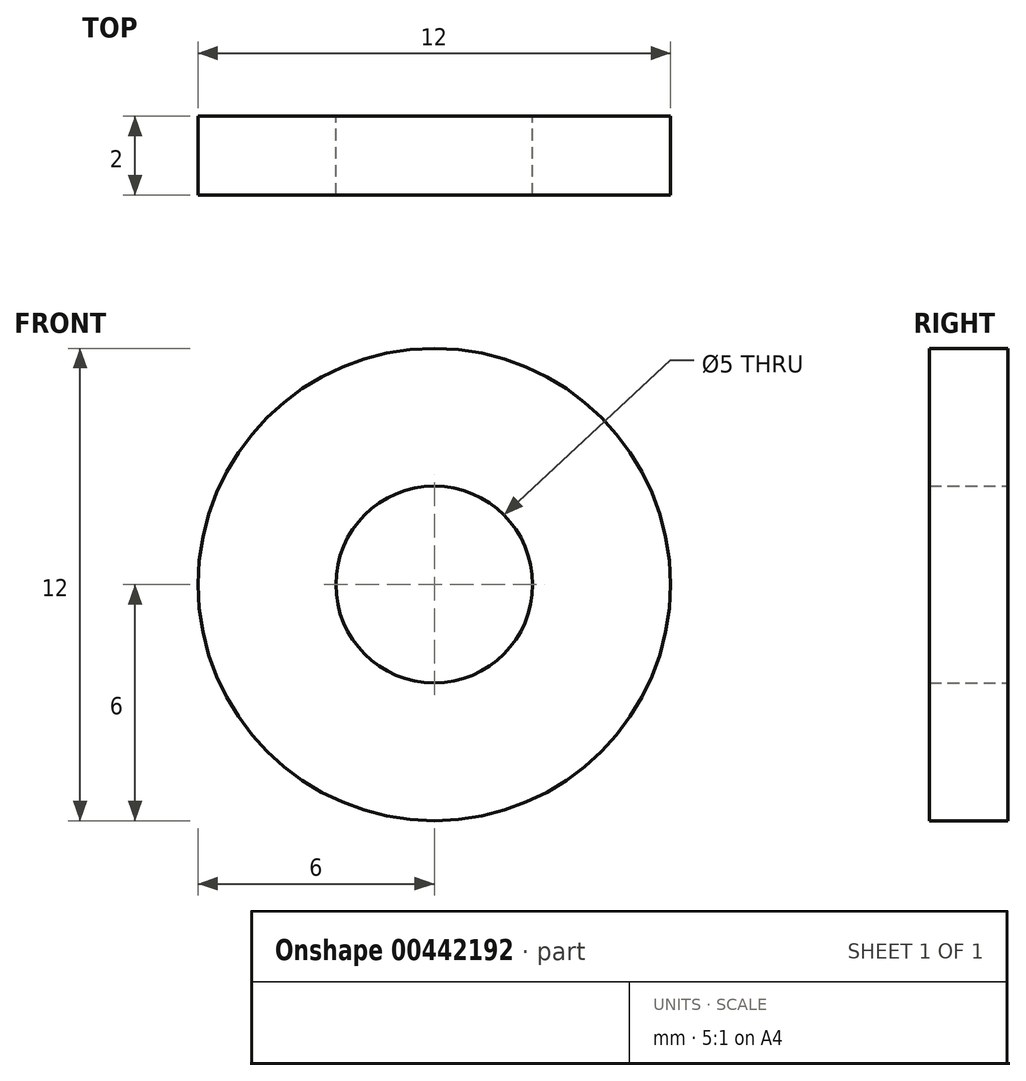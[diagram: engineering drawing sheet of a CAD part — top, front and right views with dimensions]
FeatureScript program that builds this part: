
annotation { "Feature Type Name" : "Feature", "Feature Type Description" : "" }
export const myFeature = defineFeature(function(context is Context, id is Id, definition is map)
    precondition{}
    {
        {
            var Q0;
            Q0=qCreatedBy(makeId("Front.planeOp"),FACE);
            var sketch = newSketch(context, id + "F0", { "sketchPlane" : qUnion([Q0])});
            skCircle(sketch, "E0", {"center": v(0, 0) * mm, "radius": 2.5 * mm});
            skCircle(sketch, "E1", {"center": v(0, 0) * mm, "radius": 6 * mm});
            skSolve(sketch);
        }
        {
            var Q0;
            Q0=makeQuery(id+"F0.imprint","IMPRINT",FACE,{"disambiguationData":[TD([[makeQuery(id+"F0.imprint","IMPRINT",EDGE,{"derivedFrom":sQuery(id+"F0.wireOp",EDGE,"E0")}),-1.0]])]});
            extrude(context, id + "F1", {"entities" : qUnion([Q0]), "depth" : 2 * mm});
        }
    });
